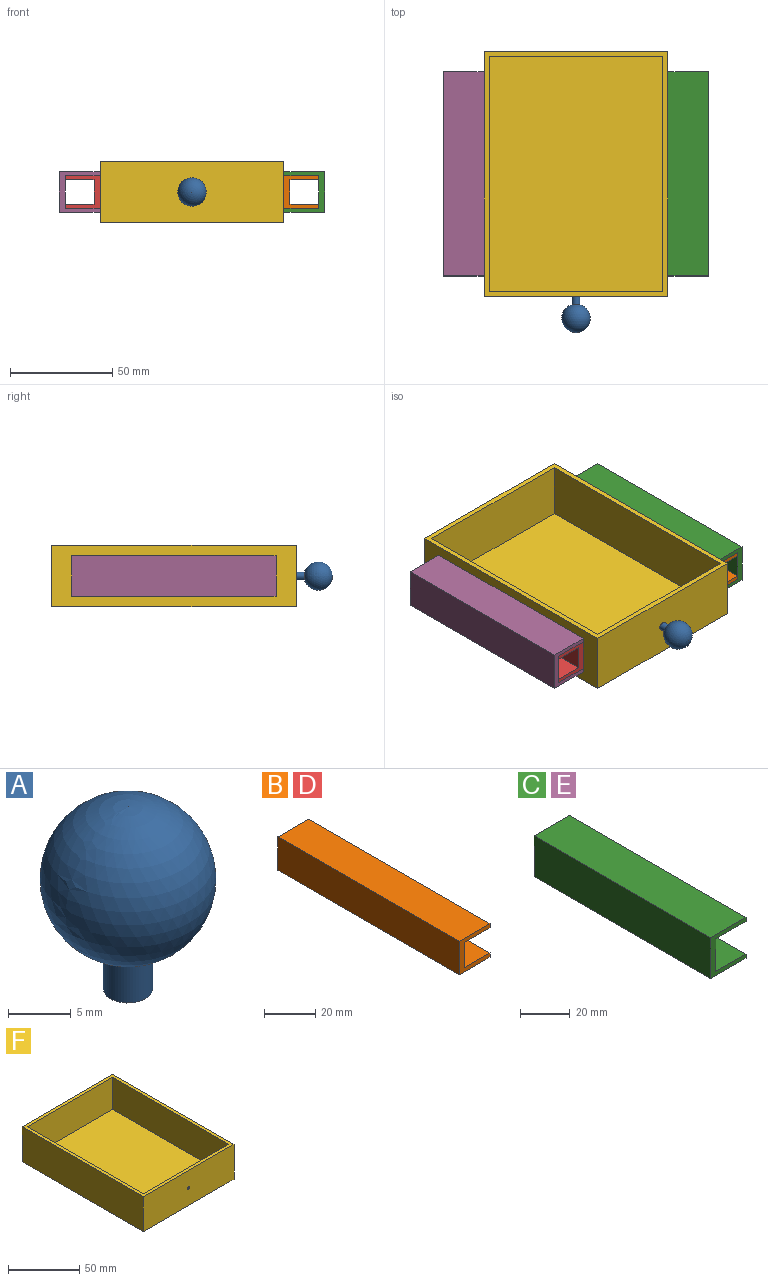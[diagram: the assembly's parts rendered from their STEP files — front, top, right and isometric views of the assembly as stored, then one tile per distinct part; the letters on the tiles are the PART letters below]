
ASSEMBLY  parts=6 mates=5
PART A: 3 faces, bbox 14x14x17.7 mm
  f0: plane 3.92x3.92mm, normal (0,0,-1), area 12.1mm2, adj f2
  f1: sphere r=7mm, area 603.4mm2, adj f2
  f2: cylinder r=1.96mm len=3.98mm, axis (0,0,-1), area 49mm2, adj f0,f1
PART B: 10 faces, bbox 17x100x16 mm
  f0: plane 100x17mm, normal (0,0,-1), area 1700mm2, adj f1,f7,f8,f9
  f1: plane 100x2mm, normal (1,0,0), area 200mm2, adj f0,f2,f8,f9
  f2: plane 100x14mm, normal (0,0,1), area 1400mm2, adj f1,f3,f8,f9
  f3: plane 100x12mm, normal (1,0,0), area 1200mm2, adj f2,f4,f8,f9
  f4: plane 100x14mm, normal (0,0,-1), area 1400mm2, adj f3,f5,f8,f9
  f5: plane 100x2mm, normal (1,0,0), area 200mm2, adj f4,f6,f8,f9
  f6: plane 100x17mm, normal (0,0,1), area 1700mm2, adj f5,f7,f8,f9
  f7: plane 100x16mm, normal (-1,0,0), area 1600mm2, adj f0,f6,f8,f9
  f8: plane 17x16mm, normal (0,-1,0), area 104mm2, adj f0,f1,f2,f3,f4,f5,f6,f7
  f9: plane 17x16mm, normal (0,1,0), area 104mm2, adj f0,f1,f2,f3,f4,f5,f6,f7
PART C: 10 faces, bbox 20x100x20 mm
  f0: plane 100x20mm, normal (0,0,-1), area 2000mm2, adj f1,f7,f8,f9
  f1: plane 100x2mm, normal (1,0,0), area 200mm2, adj f0,f2,f8,f9
  f2: plane 100x17mm, normal (0,0,1), area 1700mm2, adj f1,f3,f8,f9
  f3: plane 100x16mm, normal (1,0,0), area 1600mm2, adj f2,f4,f8,f9
  f4: plane 100x17mm, normal (0,0,-1), area 1700mm2, adj f3,f5,f8,f9
  f5: plane 100x2mm, normal (1,0,0), area 200mm2, adj f4,f6,f8,f9
  f6: plane 100x20mm, normal (0,0,1), area 2000mm2, adj f5,f7,f8,f9
  f7: plane 100x20mm, normal (-1,0,0), area 2000mm2, adj f0,f6,f8,f9
  f8: plane 20x20mm, normal (0,-1,0), area 128mm2, adj f0,f1,f2,f3,f4,f5,f6,f7
  f9: plane 20x20mm, normal (0,1,0), area 128mm2, adj f0,f1,f2,f3,f4,f5,f6,f7
PART D: same geometry as B
PART E: same geometry as C
PART F: 12 faces, bbox 90x120x30 mm
  f0: plane 120x90mm, normal (0,0,1), area 1025mm2, adj f1,f2,f3,f4,f6,f7,f8,f9
  f1: plane 90x30mm, normal (0,-1,0), area 2696.9mm2, adj f0,f2,f4,f5,f11
  f2: plane 120x30mm, normal (1,0,0), area 3600mm2, adj f0,f1,f3,f5
  f3: plane 90x30mm, normal (0,1,0), area 2700mm2, adj f0,f2,f4,f5
  f4: plane 120x30mm, normal (-1,0,0), area 3600mm2, adj f0,f1,f3,f5
  f5: plane 120x90mm, normal (0,0,-1), area 10800mm2, adj f1,f2,f3,f4
  f6: plane 85x27.5mm, normal (0,1,0), area 2334.4mm2, adj f0,f7,f9,f10,f11
  f7: plane 115x27.5mm, normal (-1,0,0), area 3162.5mm2, adj f0,f6,f8,f10
  f8: plane 85x27.5mm, normal (0,-1,0), area 2337.5mm2, adj f0,f7,f9,f10
  f9: plane 115x27.5mm, normal (1,0,0), area 3162.5mm2, adj f0,f6,f8,f10
  f10: plane 115x85mm, normal (0,0,1), area 9775mm2, adj f6,f7,f8,f9
  f11: cylinder r=1mm len=2.5mm, axis (0,-1,0), area 15.7mm2, adj f1,f6
PLACE A rot(axis=(1,0,0),90deg) t=(-3.78,-68.75,6.21)mm
PLACE B t=(49.72,51.95,6.21)mm
PLACE C rot(axis=(0,0,1),180deg) t=(51.22,-48.05,6.21)mm
PLACE D rot(axis=(0,1,0),180deg) t=(-57.28,51.95,6.21)mm
PLACE E t=(-58.78,51.95,6.21)mm
PLACE F t=(-3.78,1.95,-8.79)mm fixed
MATE fastened B.f6 <-> C.f4  axis (0,0,1) through (49.72,1.95,14.21)mm
MATE fastened B.f7 <-> F.f2  axis (-1,0,0) through (41.22,1.95,6.21)mm
MATE fastened D.f0 <-> E.f4  axis (0,0,1) through (-57.28,1.95,14.21)mm
MATE fastened D.f7 <-> F.f4  axis (1,0,0) through (-48.78,1.95,6.21)mm
MATE fastened A.f2 <-> F.f11  axis (0,1,0) through (-3.78,-58.05,6.21)mm
